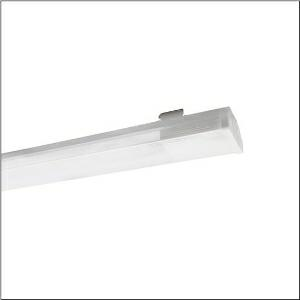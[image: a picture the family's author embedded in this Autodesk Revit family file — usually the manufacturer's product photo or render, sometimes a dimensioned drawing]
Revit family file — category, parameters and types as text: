
# Revit family: modario_31_gen_2_53bm8117u4gxc2_2154
name_source: partatom
category: Lighting Fixtures
units: mm (PartAtom-declared; Revit-internal decimal feet)

## family parameters
Cut with Voids When Loaded = No
Host = Face
Light Source = No
Part Type = Normal
Room Calculation Point = No
Round Connector Dimension = Use Diameter
Shared = No

## types (1)
- Modario 31 Gen.2 (1 x LED, 16360 lm, 90.4 W, 4000K)
    Apparent Load = 90 VA
    CIE Flux Codes = 50 78 94 90 100
    Color Rendering = 80
    Color Temperature = 4000K
    Default Elevation = 1800 mm
    Description = Modario 31 Gen.2, luminaire insert, of sheet steel, coil coated, white, length: 2.392mm, width: 81mm, height: 82mm, 8x system unit, system units: 299mm, LED rated luminous flux: 16.360lm, light colour: 840, SDCM (Standard Deviation of Colour Matching)MacAdam ≤ 3 SDCM (initial), control gear: ON/OFF, with plug, 3-pole, with phase selection, mains connection: 220..240V, AC, 50/60Hz, rated input power: 90W, through-wiring accessed according to module size, primary optical cover: cover, of PMMA, light emission: direct distribution, primary light characteristic: symmetric, protection rating (complete): IP20, protection rating (LED compartment): IP50, insulation class (complete): insulation class I (protective earthing), certification: CE, ENEC, VDE, UKCA, impact resistance: IK03, permissible ambient temperature for indoor applications: -40..+40°C, corresponds to IFS (International Featured Standards) requirements for safety and quality in the food industry, reducing of maximum allowable ambient temperature of 5°C with ceiling mounting, IP40 when using the optional accessory 5TP9018, packaging unit: 1 piece
    Height = 92 mm
    Lamp = 1 x LED
    Lamp Light Flux = 16360 lm
    Lamp Power = 90.4 W
    Lamp count = 1
    Length = 2392 mm
    Luminous efficacy = 181 lm/W
    Manufacturer = Siteco
    ModVariant = No
    Model = 53BM8117U4GXC2
    Mounting Place = Ceiling
    Mounting Type = Pendant
    Number of Poles = 1
    OnlyDefault = Yes
    Power Factor = 1
    Product Name = Modario 31 Gen.2
    Product group = luminaire insert | ceiling pendant
    ProductGroupID = 901
    Protection Class = Protection class I
    Protection Degree = IP 20
    RLX_Detail_Level = 1
    RLX_Emergency_Light_Flux = 0 lm
    RLX_Emergency_Type = 0
    RLX_Emergency_Type_DB = No
    RlxData = <blob elided: 34949 chars, md5=52f14070>
    Socket = socket
    Standby Power = 0 W
    System Light Flux = 16360 lm
    System Power = 90 W
    Type Comments = Product without accessories
    Type Image = l_1341883.jpg
    URL = http://relux.com
    VarID = ---
    Voltage = 0 V
    Weight = 0.00 kg
    Width = 81 mm

## geometry (parser evidence)
native form markers: Blend x4, Sweep x13
no freeform markers — native parametric forms only
